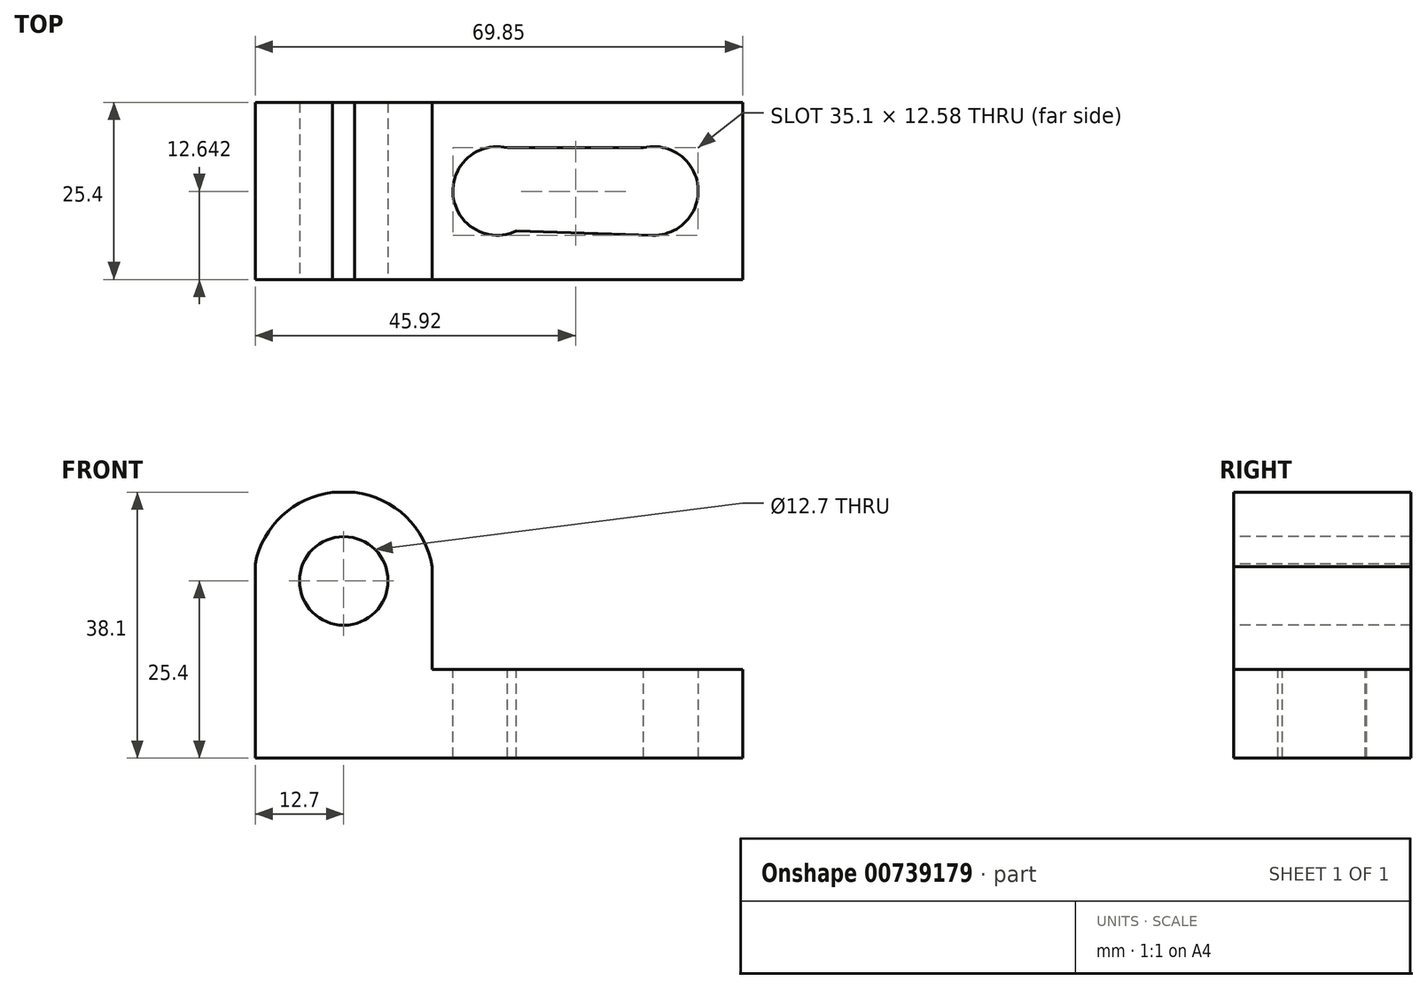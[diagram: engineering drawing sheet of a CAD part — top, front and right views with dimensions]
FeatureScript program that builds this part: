
annotation { "Feature Type Name" : "Feature", "Feature Type Description" : "" }
export const myFeature = defineFeature(function(context is Context, id is Id, definition is map)
    precondition{}
    {
        {
            var Q0;
            Q0=qCreatedBy(makeId("Front.planeOp"),FACE);
            var sketch = newSketch(context, id + "F0", { "sketchPlane" : qUnion([Q0])});
            skLineSegment(sketch, "E0", {"start": v(0, 38.1) * mm, "end": v(0, 0) * mm});
            skLineSegment(sketch, "E1", {"start": v(0, 0) * mm, "end": v(69.85, 0) * mm});
            skLineSegment(sketch, "E2", {"start": v(69.85, 0) * mm, "end": v(69.85, 12.7) * mm});
            skLineSegment(sketch, "E3", {"start": v(69.85, 12.7) * mm, "end": v(25.4, 12.7) * mm});
            skLineSegment(sketch, "E4", {"start": v(25.4, 12.7) * mm, "end": v(25.4, 38.1) * mm});
            skLineSegment(sketch, "E5", {"start": v(25.4, 38.1) * mm, "end": v(0, 38.1) * mm});
            skSolve(sketch);
        }
        {
            var Q0;
            Q0 = qSketchRegion(id + "F0", true);
            extrude(context, id + "F1", {"entities" : qUnion([Q0]), "depth" : 25.4 * mm, "offsetDistance" : 25.4 * mm});
        }
        {
            var Q0;
            Q0=makeQuery(id+"F1.opExtrude","CAP_FACE",FACE,{"disambiguationData":[OSD([sQuery(id+"F0.wireOp",EDGE,"E0"),sQuery(id+"F0.wireOp",EDGE,"E1"),sQuery(id+"F0.wireOp",EDGE,"E2"),sQuery(id+"F0.wireOp",EDGE,"E3"),sQuery(id+"F0.wireOp",EDGE,"E4"),sQuery(id+"F0.wireOp",EDGE,"E5")])],"isStart":false});
            var sketch = newSketch(context, id + "F2", { "sketchPlane" : qUnion([Q0])});
            skLineSegment(sketch, "E6", {"start": v(0, 25.4) * mm, "end": v(25.4, 25.4) * mm});
            skCircle(sketch, "E7", {"center": v(12.7, 25.4) * mm, "radius": 6.35 * mm});
            skSolve(sketch);
        }
        {
            var Q0;
            {var subQ0=sQuery(id+"F2.wireOp",EDGE,"E7");var subQ1=sQuery(id+"F2.wireOp",EDGE,"E6");var subQ2=makeQuery(id+"F2.imprint","INTERSECT",VERTEX,{"disambiguationData":[OD(0.0)],"derivedFrom":[subQ1,subQ0]});Q0=makeQuery(id+"F2.imprint","IMPRINT",FACE,{"disambiguationData":[TD([[makeQuery(id+"F2.imprint","IMPRINT",EDGE,{"disambiguationData":[TD([[subQ2,-1.0]])],"derivedFrom":subQ1}),1.0]])]});}
            var Q1;
            {var subQ0=sQuery(id+"F2.wireOp",EDGE,"E7");var subQ1=sQuery(id+"F2.wireOp",EDGE,"E6");var subQ2=makeQuery(id+"F2.imprint","INTERSECT",VERTEX,{"disambiguationData":[OD(0.0)],"derivedFrom":[subQ1,subQ0]});Q1=makeQuery(id+"F2.imprint","IMPRINT",FACE,{"disambiguationData":[TD([[makeQuery(id+"F2.imprint","IMPRINT",EDGE,{"disambiguationData":[TD([[subQ2,-1.0]])],"derivedFrom":subQ1}),-1.0]])]});}
            extrude(context, id + "F3", {"entities" : qUnion([Q0, Q1]), "operationType" : NewBodyOperationType.REMOVE, "endBound" : BoundingType.THROUGH_ALL, "oppositeDirection" : true, "depth" : 25.4 * mm, "offsetDistance" : 25.4 * mm});
        }
        {
            var Q0;
            Q0=makeQuery(id+"F1.opExtrude","CAP_FACE",FACE,{"disambiguationData":[OSD([sQuery(id+"F0.wireOp",EDGE,"E0"),sQuery(id+"F0.wireOp",EDGE,"E1"),sQuery(id+"F0.wireOp",EDGE,"E2"),sQuery(id+"F0.wireOp",EDGE,"E3"),sQuery(id+"F0.wireOp",EDGE,"E4"),sQuery(id+"F0.wireOp",EDGE,"E5")])],"isStart":false});
            var sketch = newSketch(context, id + "F4", { "sketchPlane" : qUnion([Q0])});
            skArc(sketch, "E8", {"start": v(25.4, 27.43) * mm, "mid": v(10.34, 37.99) * mm, "end": v(0, 22.77) * mm});
            skSolve(sketch);
        }
        {
            var Q0;
            {var subQ0=sQuery(id+"F4.wireOp",EDGE,"E8");var subQ1=makeQuery(id+"F1.opExtrude","CAP_EDGE",EDGE,{"disambiguationData":[OSD([sQuery(id+"F0.wireOp",EDGE,"E5")])],"isStart":false});var subQ2=makeQuery(id+"F4.imprint","INTERSECT",VERTEX,{"disambiguationData":[OD(1.0)],"derivedFrom":[subQ1,subQ0]});Q0=makeQuery(id+"F4.imprint","IMPRINT",FACE,{"disambiguationData":[TD([[makeQuery(id+"F4.imprint","IMPRINT",EDGE,{"disambiguationData":[TD([[subQ2,-1.0]])],"derivedFrom":subQ0}),-1.0]])]});}
            var Q1;
            {var subQ0=sQuery(id+"F4.wireOp",EDGE,"E8");var subQ1=makeQuery(id+"F1.opExtrude","CAP_EDGE",EDGE,{"disambiguationData":[OSD([sQuery(id+"F0.wireOp",EDGE,"E4")])],"isStart":false});var subQ2=makeQuery(id+"F4.imprint","INTERSECT",VERTEX,{"derivedFrom":[subQ1,subQ0]});Q1=makeQuery(id+"F4.imprint","IMPRINT",FACE,{"disambiguationData":[TD([[makeQuery(id+"F4.imprint","IMPRINT",EDGE,{"disambiguationData":[TD([[subQ2,-1.0]])],"derivedFrom":subQ0}),-1.0]])]});}
            extrude(context, id + "F5", {"entities" : qUnion([Q0, Q1]), "operationType" : NewBodyOperationType.REMOVE, "endBound" : BoundingType.THROUGH_ALL, "oppositeDirection" : true, "depth" : 25.4 * mm, "offsetDistance" : 25.4 * mm});
        }
        {
            var Q0;
            Q0=makeQuery(id+"F1.opExtrude","SWEPT_FACE",FACE,{"disambiguationData":[OSD([sQuery(id+"F0.wireOp",EDGE,"E3")])]});
            var sketch = newSketch(context, id + "F6", { "sketchPlane" : qUnion([Q0])});
            skCircle(sketch, "E9", {"center": v(57.15, -12.7) * mm, "radius": 6.35 * mm});
            skCircle(sketch, "E10", {"center": v(34.68, -12.7) * mm, "radius": 6.35 * mm});
            skLineSegment(sketch, "E11", {"start": v(31.56, -18.23) * mm, "end": v(56.95, -19.05) * mm});
            skLineSegment(sketch, "E12", {"start": v(33.22, -6.52) * mm, "end": v(58.62, -6.52) * mm});
            skSolve(sketch);
        }
        {
            var Q0;
            Q0 = qSketchRegion(id + "F6", true);
            extrude(context, id + "F7", {"entities" : qUnion([Q0]), "operationType" : NewBodyOperationType.REMOVE, "endBound" : BoundingType.THROUGH_ALL, "oppositeDirection" : true, "depth" : 25.4 * mm, "offsetDistance" : 25.4 * mm});
        }
    });
